# Revit family: EVF-1181S
name_source: partatom
category: Communication Devices
revit_build: Autodesk Revit 2017 (Build: 20160225_1515(x64)
units: mm (PartAtom-declared; Revit-internal decimal feet)

## family parameters
Always vertical = Yes
Cut with Voids When Loaded = No
Maintain Annotation Orientation = Yes
OmniClass Number = 23.85.10.11.11.21
OmniClass Title = Speakers
Part Type = Normal
Room Calculation Point = No
Round Connector Dimension = Use Diameter
Shared = No
Work Plane-Based = Yes

## types (6) — shared parameters
ArchitectsAndEngineersSpecs = https://www.electrovoice.com
BackLength = 426.39 mm  [stored 1.39892 ft]
Depth = 726.38 mm  [stored 2.38314 ft]
Description = EVS18SB 457mm LF Transducer. 99 dB Sensitivity, 131 dB Maximum SPL. System Rating: 400W Continuous, 1600W Peak.  (28) M10 threaded suspension points.
Disclaimer = http://resource.boschsecurity.com
FrontLength = 675.64 mm
Height = 768.55 mm
IfcExportAs = IfcBuildingElementProxy
IfcExportType = IfcBuildingElementProxyType
InstallationManual = https://www.electrovoice.com
Manufacturer = Electro Voice
ManufacturerURL = https://www.electrovoice.com
PlanningTools = https://www.electrovoice.com
ProductInformation = https://www.electrovoice.com
Uniclass2015Code = Pr_60_75_08_02
Version = 1
zero-valued in all types: Default Elevation

## per-type parameters (varying)
| type | CTN | MaterialRALColour | ModelNumber |
| EVF1181SBLB_Black_1X18_Subwoofer_System | EVF1181SBLB | RAL9004 | F.01U.272.554 |
| EVF-1181S-FGB | EVF-1181S-FGB | RAL9004 | F.01U.139.627 |
| EVF-1181S-FGW | EVF-1181S-FGW | RAL9010 | F.01U.139.628 |
| EVF1181SPBLB_Black_Weatherized_1X18_Sub | EVF1181SPBLB | RAL9004 | F.01U.272.556 |
| EVF1181SPWLB_White_Weatherized_1X18_Sub | EVF1181SPWLB | RAL9010 | F.01U.272.557 |
| EVF1181SWLB_White_1X18_Subwoofer_System | EVF1181SWLB | RAL9010 | F.01U.272.555 |

note: [stored X ft] marks values corroborated as IEEE doubles in the binary element streams (Revit-internal decimal feet)

## geometry (parser evidence)
native form markers: Blend x4, Sweep x9
no freeform markers — native parametric forms only
